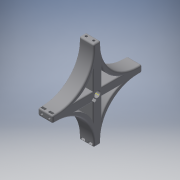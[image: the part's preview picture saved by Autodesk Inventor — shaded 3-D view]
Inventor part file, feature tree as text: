
AUTODESK INVENTOR PART (.ipt)
format: ipt  version: 2016 (Build 200138000, 138)  size: 471,552 bytes
history: native  units: mm
features: extrude x6, sketch x6, projected_geometry x5, fillet x4, pattern_circular x2, other x1, chamfer x1
ambient origin geometry x8: Origin, YZ Plane, XZ Plane, XY Plane, X Axis, Y Axis, Z Axis, Center Point
bodies: Solid1 (feature_tree)
feature tree (25):
  extrude  "Extrusion1"  Depth=9.5mm
  fillet  "Fillet1"  Radius=8.2mm
  extrude  "Extrusion3"  Depth=50.0mm
  extrude  "Extrusion4"  Depth=6.0mm
  extrude  "Extrusion5"  Depth=6.0mm
  other  "Work Axis1"
  extrude  "Extrusion6"  Depth=6.0mm
  pattern_circular  "Circular Pattern1"  Count=2  [1 undecoded]
  extrude  "Extrusion7"  Depth=1.5mm
  pattern_circular  "Circular Pattern2"  [2 undecoded]
  fillet  "Fillet2"  Radius=8.0mm
  fillet  "Fillet3"  Radius=6.0mm
  fillet  "Fillet4"  Radius=0.485281mm
  chamfer  "Chamfer1"  Distance=7.0mm
  sketch  "Sketch1"  dims[d0=120.0mm d1=9.5mm d2=8.2mm]
  sketch  "Sketch2"  dims[d3=20.0mm d4=0.0mm d5=50.0mm]
  projected_geometry  "Projected Loop2"
  sketch  "Sketch3"  dims[d6=105.0mm d7=6.0mm]
  projected_geometry  "Projected Loop3"
  sketch  "Sketch4"  dims[d10=6.0mm d11=6.0mm]
  projected_geometry  "Projected Loop4"
  sketch  "Sketch5"  dims[d12=6.0mm d13=6.0mm]
  projected_geometry  "Projected Loop5"
  sketch  "Sketch6"  dims[d14=6.0mm d15=20.0mm d16=0.0mm d17=3.0mm d18=5.9mm d19=8.0mm d21=6.0mm d22=0.485281mm d24=7.0mm d25=0.0mm d26=3.1mm d28=3.5mm d29=0.0mm d30=0.0mm d32=5.9mm d33=3.0mm d34=2.05mm d35=2.05mm d36=8.0mm d37=0.0mm d38=40.0mm d39=360.0deg d41=3.2mm d42=3.2mm d44=30.0mm d45=0.0mm d46=40.0mm d47=360.0deg d49=2.0mm d50=2.0mm d51=1.5mm d52=2.0mm d53=2.0mm d54=45.0deg]
  projected_geometry  "Projected Loop6"
note: 3 required parameter values undecoded (feature->parameter linkage not recoverable at this tier; creation-order binding heuristic only, values carry confidence <= 0.55)
